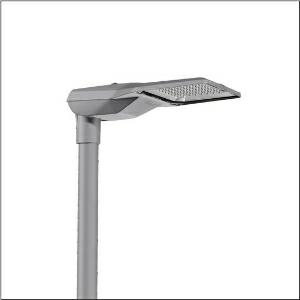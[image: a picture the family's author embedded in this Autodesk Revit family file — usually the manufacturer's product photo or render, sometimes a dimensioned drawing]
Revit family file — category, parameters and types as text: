
# Revit family: streetlight_sl_21_midi___st0_8a_5xe3c43s08nb_570f
name_source: partatom
category: Lighting Fixtures
units: mm (PartAtom-declared; Revit-internal decimal feet)

## family parameters
Cut with Voids When Loaded = No
Host = Face
Light Source = No
Part Type = Normal
Room Calculation Point = No
Round Connector Dimension = Use Diameter
Shared = No

## types (1)
- --- (1 x LED, 23710 lm, 151.2 W, 4000K)
    Apparent Load = 151 VA
    CIE Flux Codes = 41 75 97 100 100
    Color Rendering = 70
    Color Temperature = 4000K
    Default Elevation = 1800 mm
    Description = Streetlight SL 21 midi, mast luminaire, primary light control with lens, of PMMA, primary optical cover: cover, of toughened safety glass, transparent, light distribution: ST0.8a, light emission: direct distribution, primary light characteristic: asymmetric, installation type: side-entry, post-top, LED, High Power LED, rated luminous flux: 23.710lm, luminous efficacy: 157lm/W, light colour: 740, colour temperature: 4000K, control gear: D4i, control: overheat protection, constant luminous flux control, time-dependent luminous flux control, flexible luminous flux parameterisation, pre-setting: logarithmic dimming characteristic, mains connection: 230..240V, AC, 50/60Hz, start of lifetime: 151W, end of service life: 157W, reduction: 70W, luminaire housing, of diecast aluminium, powder-coated, Siteco® metallic grey (DB 702S), corrosivity category C5 mid according to DIN EN ISO 12944, please order mast flange separately, inclination adjustable: 0°, 5°, 10°, 15°, sealing non-destructively replaceable, multi-level sealing system, length: 644mm, width: 335mm, height: 110mm, mast flange for spigot size: 42mm (side-entry): 5XC10008XM4, 60/48mm (side-entry/post-top): 5XC10108XM2, 76/60mm (side-entry/post-top): 5XC10108XM1, mounting height: 4..8m, Smart Interface above, protection rating (complete): IP66, insulation class (complete): insulation class II (safety insulation), certification: CE, ENEC, ENEC+, VDE, impact resistance: IK10, permissible operating ambient temperature for outdoor applications: -40..+50°C, standard-compliant lighting for roads and squares, packaging unit: 1 piece

Light Distribution: ST0.8a
    Height = 111 mm
    Lamp = 1 x LED
    Lamp Light Flux = 23710 lm
    Lamp Power = 151.2 W
    Lamp count = 1
    Length = 644 mm
    Luminous efficacy = 157 lm/W
    Manufacturer = Siteco
    ModVariant = No
    Model = 5XE3C43S08NB
    Number of Poles = 1
    OnlyDefault = Yes
    Power Factor = 1
    Product Name = Streetlight SL 21 midi | ST0.8a
    Product group = mast luminaire | pylon top
    ProductGroupID = 6100
    Protection Class = Protection class II
    Protection Degree = IP 66
    RLX_Detail_Level = 1
    RLX_Emergency_Light_Flux = 0 lm
    RLX_Emergency_Type = 0
    RLX_Emergency_Type_DB = No
    RlxData = <blob elided: 26905 chars, md5=54422694>
    Socket = socket
    Standby Power = 0 W
    System Light Flux = 23710 lm
    System Power = 151 W
    Type Comments = factory setting: luminous flux: 100 % | dim-lin: 254 | 802 mA
    Type Image = l_1004302.jpg
    URL = http://relux.com
    VarID = @adj_190185
    Voltage = 0 V
    Weight = 0.00 kg
    Width = 336 mm

## geometry (parser evidence)
native form markers: Blend x4, Sweep x11
no freeform markers — native parametric forms only
